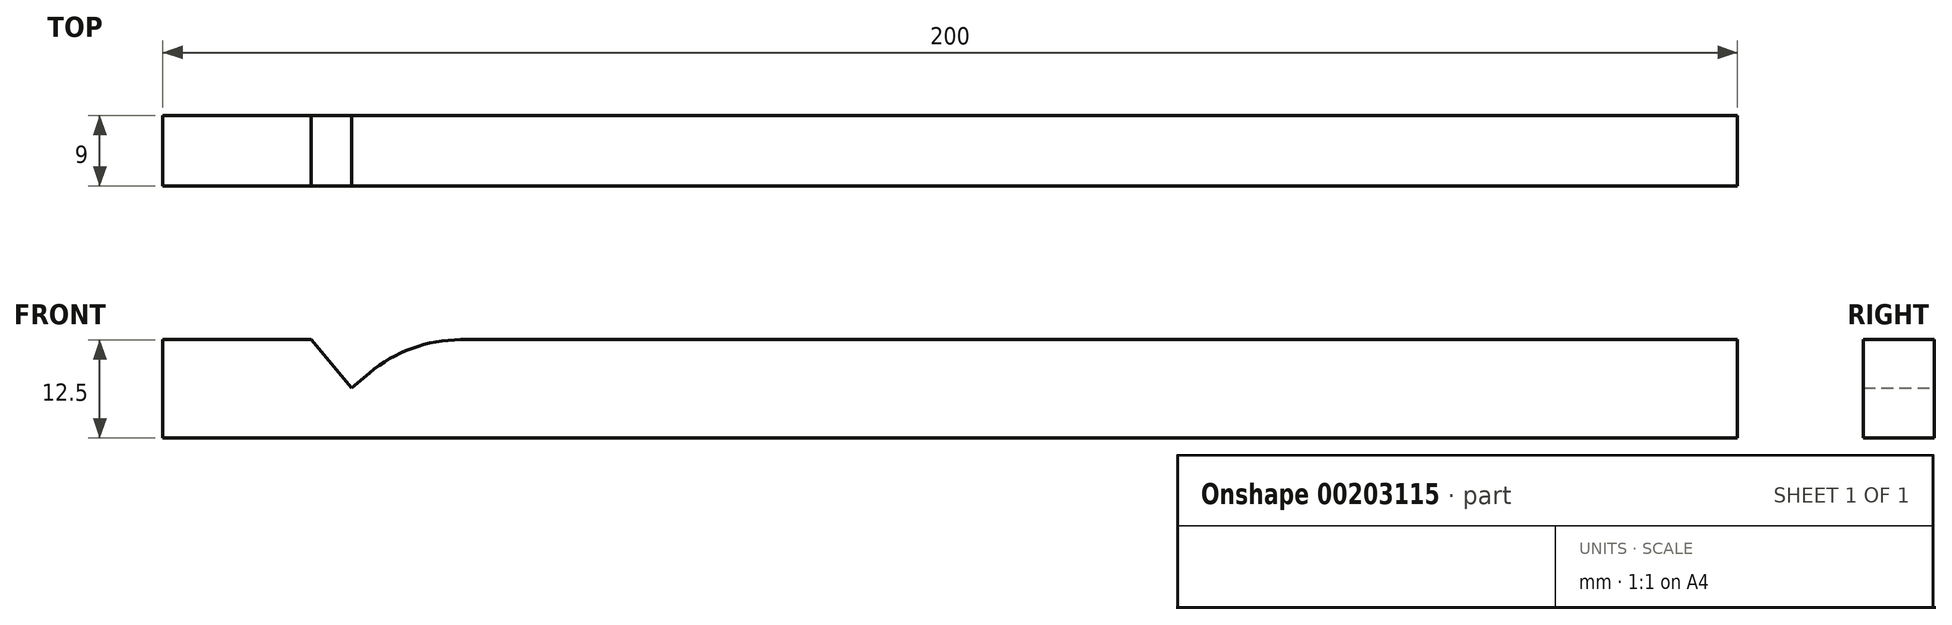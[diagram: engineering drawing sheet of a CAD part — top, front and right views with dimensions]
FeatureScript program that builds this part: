
annotation { "Feature Type Name" : "Feature", "Feature Type Description" : "" }
export const myFeature = defineFeature(function(context is Context, id is Id, definition is map)
    precondition{}
    {
        {
            var Q0;
            Q0=qCreatedBy(makeId("Front.planeOp"),FACE);
            var sketch = newSketch(context, id + "F0", { "sketchPlane" : qUnion([Q0])});
            skLineSegment(sketch, "E0.top", {"start": v(-94.07, -15.25) * mm, "end": v(105.93, -15.25) * mm});
            skLineSegment(sketch, "E0.left", {"start": v(-94.07, -2.75) * mm, "end": v(-94.07, -15.25) * mm});
            skLineSegment(sketch, "E0.right", {"start": v(105.93, -2.75) * mm, "end": v(105.93, -15.25) * mm});
            skLineSegment(sketch, "E1", {"start": v(-94.07, -2.75) * mm, "end": v(-75.24, -2.75) * mm});
            skLineSegment(sketch, "E2", {"start": v(-75.24, -2.75) * mm, "end": v(-70.09, -8.87) * mm});
            skLineSegment(sketch, "E3", {"start": v(-70.09, -8.87) * mm, "end": v(-67.83, -6.97) * mm});
            skLineSegment(sketch, "E4", {"start": v(-56.24, -2.75) * mm, "end": v(108.08, -2.75) * mm});
            skPoint(sketch, "E5.visualSharp", {"position": v(-62.8, -2.75) * mm});
            skArc(sketch, "E5.filletArc", {"start": v(-56.24, -2.75) * mm, "mid": v(-62.41, -3.84) * mm, "end": v(-67.83, -6.97) * mm});
            skSolve(sketch);
        }
        {
            var Q0;
            Q0 = qSketchRegion(id + "F0", true);
            extrude(context, id + "F1", {"entities" : qUnion([Q0]), "depth" : 9 * mm});
        }
    });
